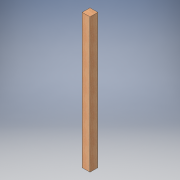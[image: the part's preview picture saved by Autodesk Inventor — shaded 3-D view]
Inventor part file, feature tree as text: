
AUTODESK INVENTOR PART (.ipt)
format: ipt  version: 2016 (Build 200138000, 138)  size: 94,720 bytes
history: native  units: in
note: dims shown in document units (in); Inventor stores cm internally (conversion verified against a paired STEP export)
features: extrude x1, sketch x1
ambient origin geometry x8: Origin, YZ Plane, XZ Plane, XY Plane, X Axis, Y Axis, Z Axis, Center Point
bodies: Solid1 (feature_tree)
feature tree (2):
  extrude  "Extrusion1"  Depth=60.0in TaperAngle=0.0deg
  sketch  "Sketch1"  dims[d0=3.5in d1=60.0in d2=0.0in]
